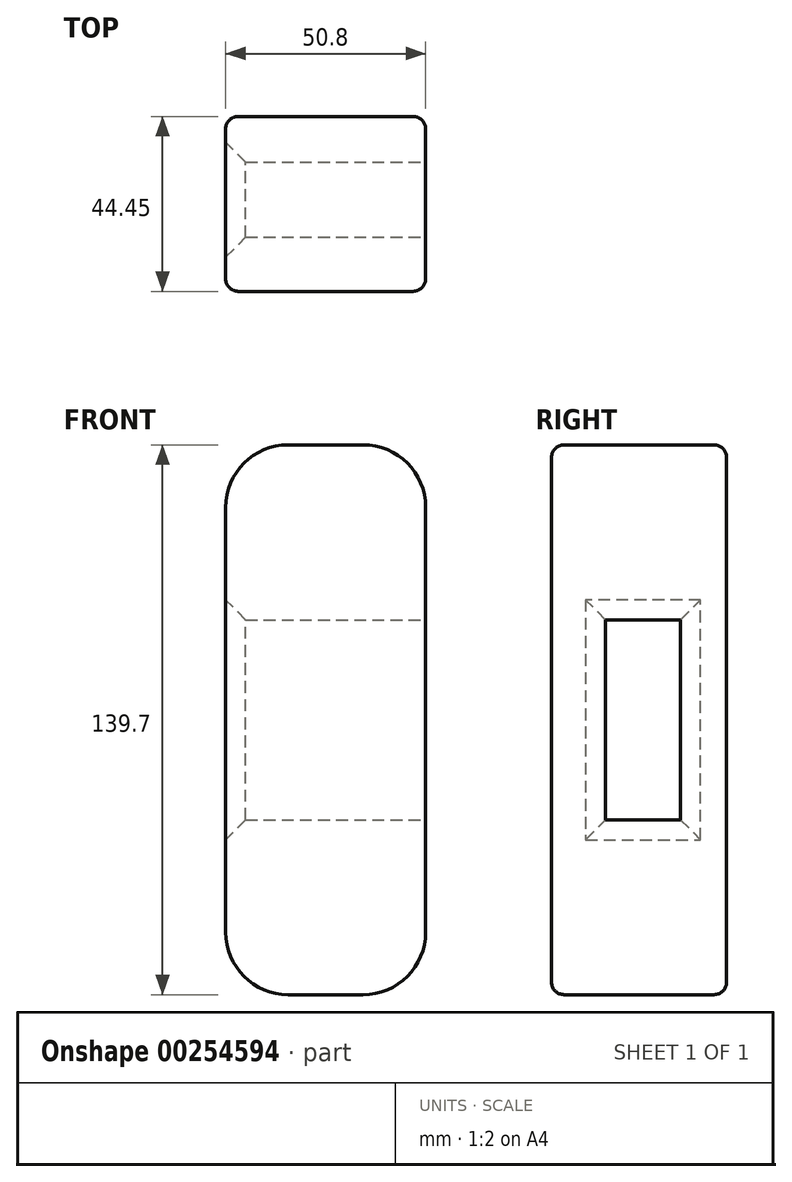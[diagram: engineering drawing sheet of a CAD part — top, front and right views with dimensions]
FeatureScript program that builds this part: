
annotation { "Feature Type Name" : "Feature", "Feature Type Description" : "" }
export const myFeature = defineFeature(function(context is Context, id is Id, definition is map)
    precondition{}
    {
        {
            var Q0;
            Q0=qCreatedBy(makeId("Front.planeOp"),FACE);
            var sketch = newSketch(context, id + "F0", { "sketchPlane" : qUnion([Q0])});
            skLineSegment(sketch, "E0.bottom", {"start": v(9.53, 69.85) * mm, "end": v(-9.53, 69.85) * mm});
            skLineSegment(sketch, "E0.top", {"start": v(9.52, -69.85) * mm, "end": v(-9.53, -69.85) * mm});
            skLineSegment(sketch, "E0.left", {"start": v(25.4, 53.98) * mm, "end": v(25.4, -53.98) * mm});
            skLineSegment(sketch, "E0.right", {"start": v(-25.4, 53.98) * mm, "end": v(-25.4, -53.98) * mm});
            skPoint(sketch, "E0.middle", {"position": v(0, 0) * mm});
            skPoint(sketch, "E1.visualSharp", {"position": v(-25.4, 69.85) * mm});
            skArc(sketch, "E1.filletArc", {"start": v(-9.53, 69.85) * mm, "mid": v(-20.75, 65.2) * mm, "end": v(-25.4, 53.98) * mm});
            skPoint(sketch, "E2.visualSharp", {"position": v(25.4, 69.85) * mm});
            skArc(sketch, "E2.filletArc", {"start": v(25.4, 53.98) * mm, "mid": v(20.75, 65.2) * mm, "end": v(9.53, 69.85) * mm});
            skPoint(sketch, "E3.visualSharp", {"position": v(-25.4, -69.85) * mm});
            skArc(sketch, "E3.filletArc", {"start": v(-25.4, -53.98) * mm, "mid": v(-20.75, -65.2) * mm, "end": v(-9.53, -69.85) * mm});
            skPoint(sketch, "E4.visualSharp", {"position": v(25.4, -69.85) * mm});
            skArc(sketch, "E4.filletArc", {"start": v(9.52, -69.85) * mm, "mid": v(20.75, -65.2) * mm, "end": v(25.4, -53.98) * mm});
            skSolve(sketch);
        }
        {
            var Q0;
            Q0=makeQuery(id+"F0.imprint","IMPRINT",FACE,{"disambiguationData":[TD([[makeQuery(id+"F0.imprint","IMPRINT",EDGE,{"derivedFrom":sQuery(id+"F0.wireOp",EDGE,"E0.bottom")}),1.0]])]});
            extrude(context, id + "F1", {"entities" : qUnion([Q0]), "depth" : 44.45 * mm});
        }
        {
            var Q0;
            Q0=makeQuery(id+"F1.opExtrude","SWEPT_FACE",FACE,{"disambiguationData":[OSD([sQuery(id+"F0.wireOp",EDGE,"E0.bottom")])]});
            var Q1;
            Q1=makeQuery(id+"F1.opExtrude","SWEPT_FACE",FACE,{"disambiguationData":[OSD([sQuery(id+"F0.wireOp",EDGE,"E0.top")])]});
            var Q2;
            Q2=makeQuery(id+"F1.opExtrude","SWEPT_FACE",FACE,{"disambiguationData":[OSD([sQuery(id+"F0.wireOp",EDGE,"E4.filletArc")])]});
            var Q3;
            Q3=makeQuery(id+"F1.opExtrude","CAP_EDGE",EDGE,{"disambiguationData":[OSD([sQuery(id+"F0.wireOp",EDGE,"E3.filletArc")])],"isStart":true});
            var Q4;
            Q4=makeQuery(id+"F1.opExtrude","SWEPT_FACE",FACE,{"disambiguationData":[OSD([sQuery(id+"F0.wireOp",EDGE,"E3.filletArc")])]});
            var Q5;
            Q5=makeQuery(id+"F1.opExtrude","SWEPT_FACE",FACE,{"disambiguationData":[OSD([sQuery(id+"F0.wireOp",EDGE,"E1.filletArc")])]});
            var Q6;
            Q6=makeQuery(id+"F1.opExtrude","SWEPT_FACE",FACE,{"disambiguationData":[OSD([sQuery(id+"F0.wireOp",EDGE,"E2.filletArc")])]});
            fillet(context, id + "F2", {"entities" : qUnion([Q0, Q1, Q2, Q3, Q4, Q5, Q6]), "radius" : 3.17 * mm, "tangentPropagation" : true, "allowEdgeOverflow" : false});
        }
        {
            var Q0;
            Q0=makeQuery(id+"F1.opExtrude","SWEPT_FACE",FACE,{"disambiguationData":[OSD([sQuery(id+"F0.wireOp",EDGE,"E0.left")])]});
            var sketch = newSketch(context, id + "F3", { "sketchPlane" : qUnion([Q0])});
            skLineSegment(sketch, "E5.bottom", {"start": v(-30.73, 25.4) * mm, "end": v(-11.68, 25.4) * mm});
            skLineSegment(sketch, "E5.top", {"start": v(-30.73, -25.4) * mm, "end": v(-11.68, -25.4) * mm});
            skLineSegment(sketch, "E5.left", {"start": v(-30.73, 25.4) * mm, "end": v(-30.73, -25.4) * mm});
            skLineSegment(sketch, "E5.right", {"start": v(-11.68, 25.4) * mm, "end": v(-11.68, -25.4) * mm});
            skPoint(sketch, "E5.middle", {"position": v(-21.2, 0) * mm});
            skSolve(sketch);
        }
        {
            var Q0;
            Q0=makeQuery(id+"F3.imprint","IMPRINT",FACE,{"disambiguationData":[TD([[makeQuery(id+"F3.imprint","IMPRINT",EDGE,{"derivedFrom":sQuery(id+"F3.wireOp",EDGE,"E5.bottom")}),-1.0]])]});
            extrude(context, id + "F4", {"entities" : qUnion([Q0]), "operationType" : NewBodyOperationType.REMOVE, "oppositeDirection" : true, "depth" : 127 * mm});
        }
        {
            var Q0;
            Q0=makeQuery(id+"F4.boolean.opBoolean","COPY",EDGE,{"derivedFrom":makeQuery(id+"F4.opExtrude","CAP_EDGE",EDGE,{"disambiguationData":[OSD([sQuery(id+"F3.wireOp",EDGE,"E5.right")])],"isStart":true})});
            var Q1;
            Q1=makeQuery(id+"F4.boolean.opBoolean","COPY",EDGE,{"derivedFrom":makeQuery(id+"F4.opExtrude","CAP_EDGE",EDGE,{"disambiguationData":[OSD([sQuery(id+"F3.wireOp",EDGE,"E5.bottom")])],"isStart":true})});
            var Q2;
            Q2=makeQuery(id+"F4.boolean.opBoolean","COPY",EDGE,{"derivedFrom":makeQuery(id+"F4.opExtrude","CAP_EDGE",EDGE,{"disambiguationData":[OSD([sQuery(id+"F3.wireOp",EDGE,"E5.left")])],"isStart":true})});
            var Q3;
            Q3=makeQuery(id+"F4.boolean.opBoolean","COPY",EDGE,{"derivedFrom":makeQuery(id+"F4.opExtrude","CAP_EDGE",EDGE,{"disambiguationData":[OSD([sQuery(id+"F3.wireOp",EDGE,"E5.top")])],"isStart":true})});
            var Q4;
            Q4=makeQuery(id+"F4.boolean.opBoolean","INTERSECT",EDGE,{"derivedFrom":[makeQuery(id+"F1.opExtrude","SWEPT_FACE",FACE,{"disambiguationData":[OSD([sQuery(id+"F0.wireOp",EDGE,"E0.right")])]}),makeQuery(id+"F4.opExtrude","SWEPT_FACE",FACE,{"disambiguationData":[OSD([sQuery(id+"F3.wireOp",EDGE,"E5.top")])]})]});
            var Q5;
            Q5=makeQuery(id+"F4.boolean.opBoolean","INTERSECT",EDGE,{"derivedFrom":[makeQuery(id+"F1.opExtrude","SWEPT_FACE",FACE,{"disambiguationData":[OSD([sQuery(id+"F0.wireOp",EDGE,"E0.right")])]}),makeQuery(id+"F4.opExtrude","SWEPT_FACE",FACE,{"disambiguationData":[OSD([sQuery(id+"F3.wireOp",EDGE,"E5.right")])]})]});
            var Q6;
            Q6=makeQuery(id+"F4.boolean.opBoolean","INTERSECT",EDGE,{"derivedFrom":[makeQuery(id+"F1.opExtrude","SWEPT_FACE",FACE,{"disambiguationData":[OSD([sQuery(id+"F0.wireOp",EDGE,"E0.right")])]}),makeQuery(id+"F4.opExtrude","SWEPT_FACE",FACE,{"disambiguationData":[OSD([sQuery(id+"F3.wireOp",EDGE,"E5.bottom")])]})]});
            var Q7;
            Q7=makeQuery(id+"F4.boolean.opBoolean","INTERSECT",EDGE,{"derivedFrom":[makeQuery(id+"F1.opExtrude","SWEPT_FACE",FACE,{"disambiguationData":[OSD([sQuery(id+"F0.wireOp",EDGE,"E0.right")])]}),makeQuery(id+"F4.opExtrude","SWEPT_FACE",FACE,{"disambiguationData":[OSD([sQuery(id+"F3.wireOp",EDGE,"E5.left")])]})]});
            chamfer(context, id + "F5", {"entities" : qUnion([Q0, Q1, Q2, Q3, Q4, Q5, Q6, Q7]), "width" : 5.08 * mm, "tangentPropagation" : true});
        }
    });
